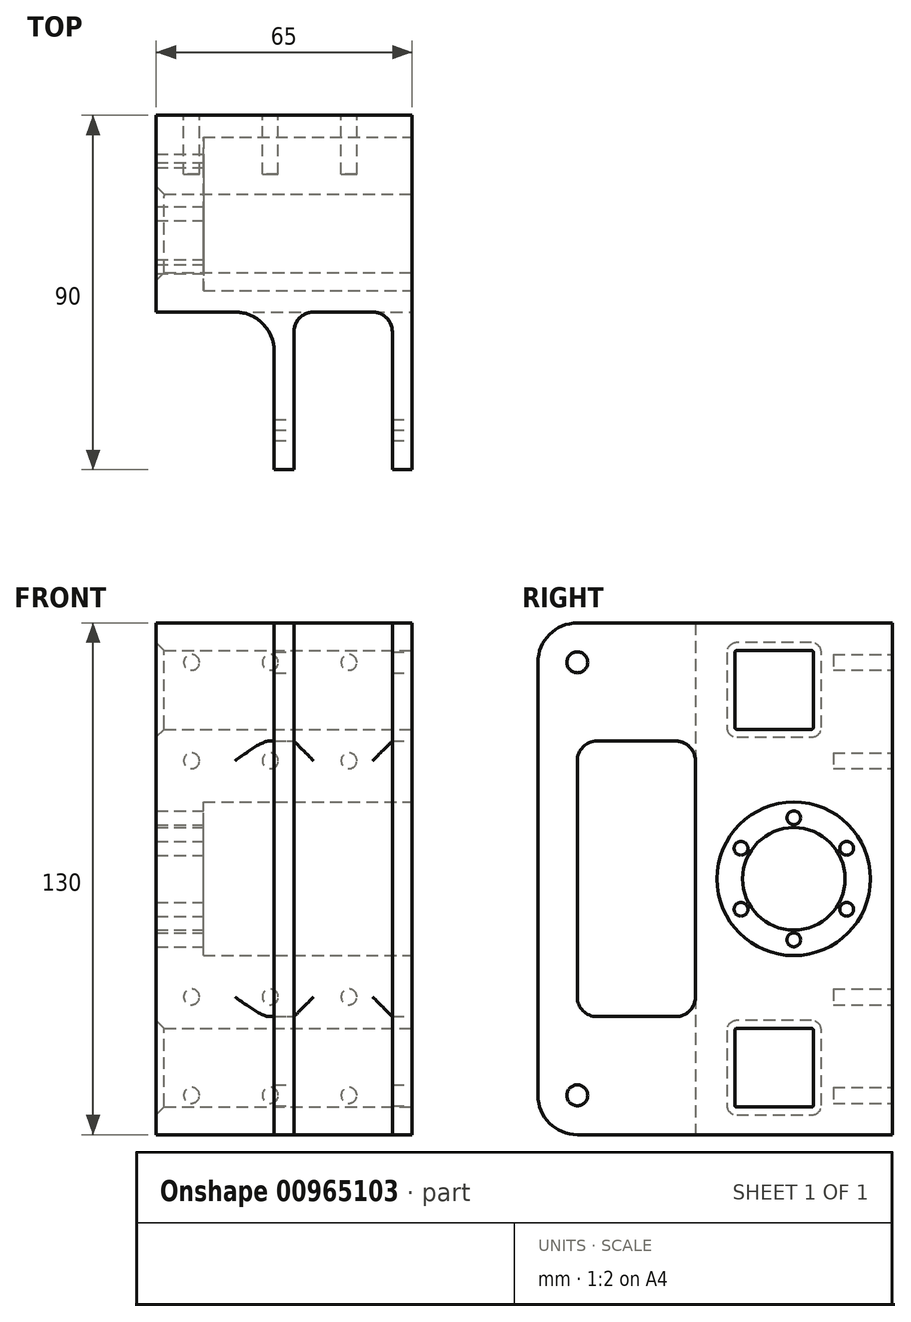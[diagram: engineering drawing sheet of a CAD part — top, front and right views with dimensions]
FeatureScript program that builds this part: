
annotation { "Feature Type Name" : "Feature", "Feature Type Description" : "" }
export const myFeature = defineFeature(function(context is Context, id is Id, definition is map)
    precondition{}
    {
        {
            var Q0;
            Q0=qCreatedBy(makeId("Top.planeOp"),FACE);
            var sketch = newSketch(context, id + "F0", { "sketchPlane" : qUnion([Q0])});
            skLineSegment(sketch, "E0", {"start": v(-30, 90) * mm, "end": v(35, 90) * mm});
            skLineSegment(sketch, "E1", {"start": v(35, 90) * mm, "end": v(35, 0) * mm});
            skLineSegment(sketch, "E2", {"start": v(35, 0) * mm, "end": v(30, 0) * mm});
            skLineSegment(sketch, "E3", {"start": v(30, 0) * mm, "end": v(30, 40) * mm});
            skLineSegment(sketch, "E4", {"start": v(30, 40) * mm, "end": v(5, 40) * mm});
            skLineSegment(sketch, "E5", {"start": v(5, 40) * mm, "end": v(5, 0) * mm});
            skLineSegment(sketch, "E6", {"start": v(5, 0) * mm, "end": v(0, 0) * mm});
            skLineSegment(sketch, "E7", {"start": v(0, 0) * mm, "end": v(0, 40) * mm});
            skLineSegment(sketch, "E8", {"start": v(0, 40) * mm, "end": v(-30, 40) * mm});
            skLineSegment(sketch, "E9", {"start": v(-30, 40) * mm, "end": v(-30, 90) * mm});
            skSolve(sketch);
        }
        {
            var Q0;
            Q0=makeQuery(id+"F0.imprint","IMPRINT",FACE,{"disambiguationData":[TD([[makeQuery(id+"F0.imprint","IMPRINT",EDGE,{"derivedFrom":sQuery(id+"F0.wireOp",EDGE,"VUWFp00N-zC5u-VRxy-L6zH-FIhfyABYxTeX")}),-1.0]])]});
            var Q1;
            Q1=makeQuery(id+"F0.imprint","IMPRINT",FACE,{"disambiguationData":[TD([[makeQuery(id+"F0.imprint","IMPRINT",EDGE,{"derivedFrom":sQuery(id+"F0.wireOp",EDGE,"E0")}),-1.0]])]});
            extrude(context, id + "F1", {"entities" : qUnion([Q0, Q1]), "depth" : 130 * mm, "offsetDistance" : 25 * mm});
        }
        {
            var Q0;
            Q0=makeQuery(id+"F1.opExtrude","SWEPT_FACE",FACE,{"disambiguationData":[OSD([sQuery(id+"F0.wireOp",EDGE,"E1")])]});
            var sketch = newSketch(context, id + "F2", { "sketchPlane" : qUnion([Q0])});
            skCircle(sketch, "E10", {"center": v(10, 120) * mm, "radius": 2.65 * mm});
            skCircle(sketch, "E11", {"center": v(10, 10) * mm, "radius": 2.65 * mm});
            skLineSegment(sketch, "E12.bottom", {"start": v(15, 30) * mm, "end": v(35, 30) * mm});
            skLineSegment(sketch, "E12.top", {"start": v(15, 100) * mm, "end": v(35, 100) * mm});
            skLineSegment(sketch, "E12.left", {"start": v(10, 35) * mm, "end": v(10, 95) * mm});
            skLineSegment(sketch, "E12.right", {"start": v(40, 35) * mm, "end": v(40, 95) * mm});
            skPoint(sketch, "E13.visualSharp", {"position": v(10, 30) * mm});
            skArc(sketch, "E13.filletArc", {"start": v(10, 35) * mm, "mid": v(11.46, 31.46) * mm, "end": v(15, 30) * mm});
            skPoint(sketch, "E14.visualSharp", {"position": v(10, 100) * mm});
            skArc(sketch, "E14.filletArc", {"start": v(15, 100) * mm, "mid": v(11.46, 98.54) * mm, "end": v(10, 95) * mm});
            skPoint(sketch, "E15.visualSharp", {"position": v(40, 100) * mm});
            skArc(sketch, "E15.filletArc", {"start": v(40, 95) * mm, "mid": v(38.54, 98.54) * mm, "end": v(35, 100) * mm});
            skPoint(sketch, "E16.visualSharp", {"position": v(40, 30) * mm});
            skArc(sketch, "E16.filletArc", {"start": v(35, 30) * mm, "mid": v(38.54, 31.46) * mm, "end": v(40, 35) * mm});
            skCircle(sketch, "E17", {"center": v(65, 65) * mm, "radius": 19.5 * mm});
            skCircle(sketch, "E18", {"center": v(65, 65) * mm, "radius": 13 * mm});
            skCircle(sketch, "E19", {"center": v(65, 49.5) * mm, "radius": 1.75 * mm});
            skCircle(sketch, "E20.1.0", {"center": v(78.42, 57.25) * mm, "radius": 1.75 * mm});
            skCircle(sketch, "E20.2.0", {"center": v(78.42, 72.75) * mm, "radius": 1.75 * mm});
            skCircle(sketch, "E20.3.0", {"center": v(65, 80.5) * mm, "radius": 1.75 * mm});
            skCircle(sketch, "E20.4.0", {"center": v(51.58, 72.75) * mm, "radius": 1.75 * mm});
            skCircle(sketch, "E20.5.0", {"center": v(51.58, 57.25) * mm, "radius": 1.75 * mm});
            skLineSegment(sketch, "E21", {"start": v(50, 7.5) * mm, "end": v(50, 26.5) * mm});
            skLineSegment(sketch, "E22", {"start": v(50.5, 27) * mm, "end": v(69.5, 27) * mm});
            skLineSegment(sketch, "E23", {"start": v(70, 26.5) * mm, "end": v(70, 7.5) * mm});
            skLineSegment(sketch, "E24", {"start": v(69.5, 7) * mm, "end": v(50.5, 7) * mm});
            skPoint(sketch, "E25.visualSharp", {"position": v(50, 7) * mm});
            skArc(sketch, "E25.filletArc", {"start": v(50, 7.5) * mm, "mid": v(50.15, 7.15) * mm, "end": v(50.5, 7) * mm});
            skPoint(sketch, "E26.visualSharp", {"position": v(50, 27) * mm});
            skArc(sketch, "E26.filletArc", {"start": v(50.5, 27) * mm, "mid": v(50.15, 26.85) * mm, "end": v(50, 26.5) * mm});
            skPoint(sketch, "E27.visualSharp", {"position": v(70, 27) * mm});
            skArc(sketch, "E27.filletArc", {"start": v(70, 26.5) * mm, "mid": v(69.85, 26.85) * mm, "end": v(69.5, 27) * mm});
            skPoint(sketch, "E28.visualSharp", {"position": v(70, 7) * mm});
            skArc(sketch, "E28.filletArc", {"start": v(69.5, 7) * mm, "mid": v(69.85, 7.15) * mm, "end": v(70, 7.5) * mm});
            skLineSegment(sketch, "E29.bottom", {"start": v(50.5, 103) * mm, "end": v(69.5, 103) * mm});
            skLineSegment(sketch, "E29.top", {"start": v(50.5, 123) * mm, "end": v(69.5, 123) * mm});
            skLineSegment(sketch, "E29.left", {"start": v(50, 103.5) * mm, "end": v(50, 122.5) * mm});
            skLineSegment(sketch, "E29.right", {"start": v(70, 103.5) * mm, "end": v(70, 122.5) * mm});
            skPoint(sketch, "E30.visualSharp", {"position": v(50, 103) * mm});
            skArc(sketch, "E30.filletArc", {"start": v(50, 103.5) * mm, "mid": v(50.15, 103.15) * mm, "end": v(50.5, 103) * mm});
            skPoint(sketch, "E31.visualSharp", {"position": v(50, 123) * mm});
            skArc(sketch, "E31.filletArc", {"start": v(50.5, 123) * mm, "mid": v(50.15, 122.85) * mm, "end": v(50, 122.5) * mm});
            skPoint(sketch, "E32.visualSharp", {"position": v(70, 123) * mm});
            skArc(sketch, "E32.filletArc", {"start": v(70, 122.5) * mm, "mid": v(69.85, 122.85) * mm, "end": v(69.5, 123) * mm});
            skPoint(sketch, "E33.visualSharp", {"position": v(70, 103) * mm});
            skArc(sketch, "E33.filletArc", {"start": v(69.5, 103) * mm, "mid": v(69.85, 103.15) * mm, "end": v(70, 103.5) * mm});
            skLineSegment(sketch, "E34", {"start": v(65, 49.5) * mm, "end": v(65, 80.5) * mm, "construction": true});
            skSolve(sketch);
        }
        {
            var Q0;
            Q0=makeQuery(id+"F2.imprint","IMPRINT",FACE,{"disambiguationData":[TD([[makeQuery(id+"F2.imprint","IMPRINT",EDGE,{"derivedFrom":sQuery(id+"F2.wireOp",EDGE,"E10")}),1.0]])]});
            var Q1;
            Q1=makeQuery(id+"F2.imprint","IMPRINT",FACE,{"disambiguationData":[TD([[makeQuery(id+"F2.imprint","IMPRINT",EDGE,{"derivedFrom":sQuery(id+"F2.wireOp",EDGE,"E11")}),1.0]])]});
            var Q2;
            Q2=makeQuery(id+"F2.imprint","IMPRINT",FACE,{"disambiguationData":[TD([[makeQuery(id+"F2.imprint","IMPRINT",EDGE,{"derivedFrom":sQuery(id+"F2.wireOp",EDGE,"3LTuBmyO-ozfh-fqRh-PIQ7-Bl0UIvrHlnbr")}),1.0]])]});
            var Q3;
            Q3=makeQuery(id+"F2.imprint","IMPRINT",FACE,{"disambiguationData":[TD([[makeQuery(id+"F2.imprint","IMPRINT",EDGE,{"derivedFrom":sQuery(id+"F2.wireOp",EDGE,"pFQCxoCr-TVhD-4vzE-fEfu-qZQpqEUeKmVJ")}),1.0]])]});
            var Q4;
            Q4=makeQuery(id+"F2.imprint","IMPRINT",FACE,{"disambiguationData":[TD([[makeQuery(id+"F2.imprint","IMPRINT",EDGE,{"derivedFrom":sQuery(id+"F2.wireOp",EDGE,"E12.bottom")}),1.0]])]});
            var Q5;
            Q5=makeQuery(id+"F2.imprint","IMPRINT",FACE,{"disambiguationData":[TD([[makeQuery(id+"F2.imprint","IMPRINT",EDGE,{"derivedFrom":sQuery(id+"F2.wireOp",EDGE,"e3bf7061-d5e7-40bd-b819-898350ce238f")}),1.0]])]});
            var Q6;
            Q6=makeQuery(id+"F2.imprint","IMPRINT",FACE,{"disambiguationData":[TD([[makeQuery(id+"F2.imprint","IMPRINT",EDGE,{"derivedFrom":sQuery(id+"F2.wireOp",EDGE,"432fe903-bb82-42f1-b88f-b60232efa730")}),1.0]])]});
            var Q7;
            Q7=makeQuery(id+"F2.imprint","IMPRINT",FACE,{"disambiguationData":[TD([[makeQuery(id+"F2.imprint","IMPRINT",EDGE,{"derivedFrom":sQuery(id+"F2.wireOp",EDGE,"E18")}),1.0]])]});
            var Q8;
            Q8=makeQuery(id+"F2.imprint","IMPRINT",FACE,{"disambiguationData":[TD([[makeQuery(id+"F2.imprint","IMPRINT",EDGE,{"derivedFrom":sQuery(id+"F2.wireOp",EDGE,"E19")}),1.0]])]});
            var Q9;
            Q9=makeQuery(id+"F2.imprint","IMPRINT",FACE,{"disambiguationData":[TD([[makeQuery(id+"F2.imprint","IMPRINT",EDGE,{"derivedFrom":sQuery(id+"F2.wireOp",EDGE,"E20.7.0")}),1.0]])]});
            var Q10;
            Q10=makeQuery(id+"F2.imprint","IMPRINT",FACE,{"disambiguationData":[TD([[makeQuery(id+"F2.imprint","IMPRINT",EDGE,{"derivedFrom":sQuery(id+"F2.wireOp",EDGE,"E20.6.0")}),1.0]])]});
            var Q11;
            Q11=makeQuery(id+"F2.imprint","IMPRINT",FACE,{"disambiguationData":[TD([[makeQuery(id+"F2.imprint","IMPRINT",EDGE,{"derivedFrom":sQuery(id+"F2.wireOp",EDGE,"E20.5.0")}),1.0]])]});
            var Q12;
            Q12=makeQuery(id+"F2.imprint","IMPRINT",FACE,{"disambiguationData":[TD([[makeQuery(id+"F2.imprint","IMPRINT",EDGE,{"derivedFrom":sQuery(id+"F2.wireOp",EDGE,"E20.4.0")}),1.0]])]});
            var Q13;
            Q13=makeQuery(id+"F2.imprint","IMPRINT",FACE,{"disambiguationData":[TD([[makeQuery(id+"F2.imprint","IMPRINT",EDGE,{"derivedFrom":sQuery(id+"F2.wireOp",EDGE,"E20.3.0")}),1.0]])]});
            var Q14;
            Q14=makeQuery(id+"F2.imprint","IMPRINT",FACE,{"disambiguationData":[TD([[makeQuery(id+"F2.imprint","IMPRINT",EDGE,{"derivedFrom":sQuery(id+"F2.wireOp",EDGE,"E20.2.0")}),1.0]])]});
            var Q15;
            Q15=makeQuery(id+"F2.imprint","IMPRINT",FACE,{"disambiguationData":[TD([[makeQuery(id+"F2.imprint","IMPRINT",EDGE,{"derivedFrom":sQuery(id+"F2.wireOp",EDGE,"E20.1.0")}),1.0]])]});
            var Q16;
            Q16=makeQuery(id+"F2.imprint","IMPRINT",FACE,{"disambiguationData":[TD([[makeQuery(id+"F2.imprint","IMPRINT",EDGE,{"derivedFrom":sQuery(id+"F2.wireOp",EDGE,"E21")}),-1.0]])]});
            var Q17;
            Q17=makeQuery(id+"F2.imprint","IMPRINT",FACE,{"disambiguationData":[TD([[makeQuery(id+"F2.imprint","IMPRINT",EDGE,{"derivedFrom":sQuery(id+"F2.wireOp",EDGE,"E29.bottom")}),1.0]])]});
            extrude(context, id + "F3", {"entities" : qUnion([Q0, Q1, Q2, Q3, Q4, Q5, Q6, Q7, Q8, Q9, Q10, Q11, Q12, Q13, Q14, Q15, Q16, Q17]), "operationType" : NewBodyOperationType.REMOVE, "oppositeDirection" : true, "depth" : 80 * mm, "offsetDistance" : 25 * mm});
        }
        {
            var Q0;
            Q0=makeQuery(id+"F2.imprint","IMPRINT",FACE,{"disambiguationData":[TD([[makeQuery(id+"F2.imprint","IMPRINT",EDGE,{"derivedFrom":sQuery(id+"F2.wireOp",EDGE,"E17")}),1.0]])]});
            extrude(context, id + "F4", {"entities" : qUnion([Q0]), "operationType" : NewBodyOperationType.REMOVE, "oppositeDirection" : true, "depth" : 53 * mm, "offsetDistance" : 25 * mm});
        }
        {
            var Q0;
            Q0=makeQuery(id+"F1.opExtrude","CAP_EDGE",EDGE,{"disambiguationData":[OSD([sQuery(id+"F0.wireOp",EDGE,"E2")])],"isStart":false});
            var Q1;
            Q1=makeQuery(id+"F1.opExtrude","CAP_EDGE",EDGE,{"disambiguationData":[OSD([sQuery(id+"F0.wireOp",EDGE,"E6")])],"isStart":false});
            var Q2;
            Q2=makeQuery(id+"F1.opExtrude","CAP_EDGE",EDGE,{"disambiguationData":[OSD([sQuery(id+"F0.wireOp",EDGE,"E2")])],"isStart":true});
            var Q3;
            Q3=makeQuery(id+"F1.opExtrude","CAP_EDGE",EDGE,{"disambiguationData":[OSD([sQuery(id+"F0.wireOp",EDGE,"E6")])],"isStart":true});
            var Q4;
            {var subQ0=sQuery(id+"F0.wireOp",EDGE,"E8");var subQ1=sQuery(id+"F0.wireOp",EDGE,"E7");Q4=makeQuery(id+"F3.boolean.opBoolean","SPLIT",EDGE,{"disambiguationData":[TD([makeQuery(id+"F3.opExtrude","SWEPT_FACE",FACE,{"disambiguationData":[OSD([sQuery(id+"F2.wireOp",EDGE,"E15.filletArc")])]})])],"derivedFrom":makeQuery(id+"F1.opExtrude","SWEPT_EDGE",EDGE,{"disambiguationData":[OSD([subQ1,subQ0])]})});}
            var Q5;
            {var subQ0=sQuery(id+"F0.wireOp",EDGE,"E8");var subQ1=sQuery(id+"F0.wireOp",EDGE,"E7");Q5=makeQuery(id+"F3.boolean.opBoolean","SPLIT",EDGE,{"disambiguationData":[TD([makeQuery(id+"F3.opExtrude","SWEPT_FACE",FACE,{"disambiguationData":[OSD([sQuery(id+"F2.wireOp",EDGE,"E16.filletArc")])]})])],"derivedFrom":makeQuery(id+"F1.opExtrude","SWEPT_EDGE",EDGE,{"disambiguationData":[OSD([subQ1,subQ0])]})});}
            fillet(context, id + "F5", {"entities" : qUnion([Q0, Q1, Q2, Q3, Q4, Q5]), "tangentPropagation" : true, "radius" : 10 * mm, "defaultsChanged" : false, "vertexSettings" : [], "allowEdgeOverflow" : false});
        }
        {
            var Q0;
            {var subQ1=sQuery(id+"F0.wireOp",EDGE,"E4");var subQ2=sQuery(id+"F0.wireOp",EDGE,"E5");Q0=makeQuery(id+"F3.boolean.opBoolean","SPLIT",EDGE,{"disambiguationData":[TD([makeQuery(id+"F3.opExtrude","SWEPT_FACE",FACE,{"disambiguationData":[OSD([sQuery(id+"F2.wireOp",EDGE,"E15.filletArc")])]})])],"derivedFrom":makeQuery(id+"F1.opExtrude","SWEPT_EDGE",EDGE,{"disambiguationData":[OSD([subQ1,subQ2])]})});}
            var Q1;
            {var subQ1=sQuery(id+"F0.wireOp",EDGE,"E5");var subQ2=sQuery(id+"F0.wireOp",EDGE,"E4");Q1=makeQuery(id+"F3.boolean.opBoolean","SPLIT",EDGE,{"disambiguationData":[TD([makeQuery(id+"F3.opExtrude","SWEPT_FACE",FACE,{"disambiguationData":[OSD([sQuery(id+"F2.wireOp",EDGE,"E16.filletArc")])]})])],"derivedFrom":makeQuery(id+"F1.opExtrude","SWEPT_EDGE",EDGE,{"disambiguationData":[OSD([subQ2,subQ1])]})});}
            var Q2;
            {var subQ0=sQuery(id+"F0.wireOp",EDGE,"E4");var subQ2=sQuery(id+"F0.wireOp",EDGE,"E3");Q2=makeQuery(id+"F3.boolean.opBoolean","SPLIT",EDGE,{"disambiguationData":[TD([makeQuery(id+"F3.opExtrude","SWEPT_FACE",FACE,{"disambiguationData":[OSD([sQuery(id+"F2.wireOp",EDGE,"E15.filletArc")])]})])],"derivedFrom":makeQuery(id+"F1.opExtrude","SWEPT_EDGE",EDGE,{"disambiguationData":[OSD([subQ2,subQ0])]})});}
            var Q3;
            {var subQ1=sQuery(id+"F0.wireOp",EDGE,"E3");var subQ2=sQuery(id+"F0.wireOp",EDGE,"E4");Q3=makeQuery(id+"F3.boolean.opBoolean","SPLIT",EDGE,{"disambiguationData":[TD([makeQuery(id+"F3.opExtrude","SWEPT_FACE",FACE,{"disambiguationData":[OSD([sQuery(id+"F2.wireOp",EDGE,"E16.filletArc")])]})])],"derivedFrom":makeQuery(id+"F1.opExtrude","SWEPT_EDGE",EDGE,{"disambiguationData":[OSD([subQ1,subQ2])]})});}
            fillet(context, id + "F6", {"entities" : qUnion([Q0, Q1, Q2, Q3]), "tangentPropagation" : true, "radius" : 5 * mm, "defaultsChanged" : false, "vertexSettings" : [], "allowEdgeOverflow" : false});
        }
        {
            var Q0;
            Q0=makeQuery(id+"F3.boolean.opBoolean","INTERSECT",EDGE,{"derivedFrom":[makeQuery(id+"F1.opExtrude","SWEPT_FACE",FACE,{"disambiguationData":[OSD([sQuery(id+"F0.wireOp",EDGE,"E9")])]}),makeQuery(id+"F3.opExtrude","SWEPT_FACE",FACE,{"disambiguationData":[OSD([sQuery(id+"F2.wireOp",EDGE,"E29.top")])]})]});
            var Q1;
            Q1=makeQuery(id+"F3.boolean.opBoolean","INTERSECT",EDGE,{"derivedFrom":[makeQuery(id+"F1.opExtrude","SWEPT_FACE",FACE,{"disambiguationData":[OSD([sQuery(id+"F0.wireOp",EDGE,"E9")])]}),makeQuery(id+"F3.opExtrude","SWEPT_FACE",FACE,{"disambiguationData":[OSD([sQuery(id+"F2.wireOp",EDGE,"E22")])]})]});
            chamfer(context, id + "F7", {"entities" : qUnion([Q0, Q1]), "width" : 2 * mm, "tangentPropagation" : true});
        }
        {
            var Q0;
            Q0=makeQuery(id+"F1.opExtrude","SWEPT_FACE",FACE,{"disambiguationData":[OSD([sQuery(id+"F0.wireOp",EDGE,"E0")])]});
            var sketch = newSketch(context, id + "F8", { "sketchPlane" : qUnion([Q0])});
            skCircle(sketch, "E35", {"center": v(21, 10) * mm, "radius": 2 * mm});
            skCircle(sketch, "E36.0.1.0", {"center": v(21, 35) * mm, "radius": 2 * mm});
            skCircle(sketch, "E36.1.0.0", {"center": v(1, 10) * mm, "radius": 2 * mm});
            skCircle(sketch, "E36.1.1.0", {"center": v(1, 35) * mm, "radius": 2 * mm});
            skCircle(sketch, "E36.2.0.0", {"center": v(-19, 10) * mm, "radius": 2 * mm});
            skCircle(sketch, "E36.2.1.0", {"center": v(-19, 35) * mm, "radius": 2 * mm});
            skLineSegment(sketch, "E36.direction1", {"start": v(21, 10) * mm, "end": v(1, 10) * mm, "construction": true});
            skLineSegment(sketch, "E36.direction2", {"start": v(21, 10) * mm, "end": v(21, 35) * mm, "construction": true});
            skCircle(sketch, "E37", {"center": v(21, 120) * mm, "radius": 2 * mm});
            skCircle(sketch, "E38.0.1.0", {"center": v(21, 95) * mm, "radius": 2 * mm});
            skCircle(sketch, "E38.1.0.0", {"center": v(1, 120) * mm, "radius": 2 * mm});
            skCircle(sketch, "E38.1.1.0", {"center": v(1, 95) * mm, "radius": 2 * mm});
            skCircle(sketch, "E38.2.0.0", {"center": v(-19, 120) * mm, "radius": 2 * mm});
            skCircle(sketch, "E38.2.1.0", {"center": v(-19, 95) * mm, "radius": 2 * mm});
            skLineSegment(sketch, "E38.direction1", {"start": v(21, 120) * mm, "end": v(1, 120) * mm, "construction": true});
            skLineSegment(sketch, "E38.direction2", {"start": v(21, 120) * mm, "end": v(21, 95) * mm, "construction": true});
            skSolve(sketch);
        }
        {
            var Q0;
            Q0=makeQuery(id+"F8.imprint","IMPRINT",FACE,{"disambiguationData":[TD([[makeQuery(id+"F8.imprint","IMPRINT",EDGE,{"derivedFrom":sQuery(id+"F8.wireOp",EDGE,"E35")}),1.0]])]});
            var Q1;
            Q1=makeQuery(id+"F8.imprint","IMPRINT",FACE,{"disambiguationData":[TD([[makeQuery(id+"F8.imprint","IMPRINT",EDGE,{"derivedFrom":sQuery(id+"F8.wireOp",EDGE,"E36.1.0.0")}),1.0]])]});
            var Q2;
            Q2=makeQuery(id+"F8.imprint","IMPRINT",FACE,{"disambiguationData":[TD([[makeQuery(id+"F8.imprint","IMPRINT",EDGE,{"derivedFrom":sQuery(id+"F8.wireOp",EDGE,"E36.2.0.0")}),1.0]])]});
            var Q3;
            Q3=makeQuery(id+"F8.imprint","IMPRINT",FACE,{"disambiguationData":[TD([[makeQuery(id+"F8.imprint","IMPRINT",EDGE,{"derivedFrom":sQuery(id+"F8.wireOp",EDGE,"E36.1.1.0")}),1.0]])]});
            var Q4;
            Q4=makeQuery(id+"F8.imprint","IMPRINT",FACE,{"disambiguationData":[TD([[makeQuery(id+"F8.imprint","IMPRINT",EDGE,{"derivedFrom":sQuery(id+"F8.wireOp",EDGE,"E36.2.1.0")}),1.0]])]});
            var Q5;
            Q5=makeQuery(id+"F8.imprint","IMPRINT",FACE,{"disambiguationData":[TD([[makeQuery(id+"F8.imprint","IMPRINT",EDGE,{"derivedFrom":sQuery(id+"F8.wireOp",EDGE,"E36.0.1.0")}),1.0]])]});
            var Q6;
            Q6=makeQuery(id+"F8.imprint","IMPRINT",FACE,{"disambiguationData":[TD([[makeQuery(id+"F8.imprint","IMPRINT",EDGE,{"derivedFrom":sQuery(id+"F8.wireOp",EDGE,"E38.0.1.0")}),1.0]])]});
            var Q7;
            Q7=makeQuery(id+"F8.imprint","IMPRINT",FACE,{"disambiguationData":[TD([[makeQuery(id+"F8.imprint","IMPRINT",EDGE,{"derivedFrom":sQuery(id+"F8.wireOp",EDGE,"E38.1.1.0")}),1.0]])]});
            var Q8;
            Q8=makeQuery(id+"F8.imprint","IMPRINT",FACE,{"disambiguationData":[TD([[makeQuery(id+"F8.imprint","IMPRINT",EDGE,{"derivedFrom":sQuery(id+"F8.wireOp",EDGE,"E38.2.1.0")}),1.0]])]});
            var Q9;
            Q9=makeQuery(id+"F8.imprint","IMPRINT",FACE,{"disambiguationData":[TD([[makeQuery(id+"F8.imprint","IMPRINT",EDGE,{"derivedFrom":sQuery(id+"F8.wireOp",EDGE,"E38.2.0.0")}),1.0]])]});
            var Q10;
            Q10=makeQuery(id+"F8.imprint","IMPRINT",FACE,{"disambiguationData":[TD([[makeQuery(id+"F8.imprint","IMPRINT",EDGE,{"derivedFrom":sQuery(id+"F8.wireOp",EDGE,"E38.1.0.0")}),1.0]])]});
            var Q11;
            Q11=makeQuery(id+"F8.imprint","IMPRINT",FACE,{"disambiguationData":[TD([[makeQuery(id+"F8.imprint","IMPRINT",EDGE,{"derivedFrom":sQuery(id+"F8.wireOp",EDGE,"E37")}),1.0]])]});
            extrude(context, id + "F9", {"entities" : qUnion([Q0, Q1, Q2, Q3, Q4, Q5, Q6, Q7, Q8, Q9, Q10, Q11]), "operationType" : NewBodyOperationType.REMOVE, "oppositeDirection" : true, "depth" : 15 * mm, "offsetDistance" : 25 * mm});
        }
    });
